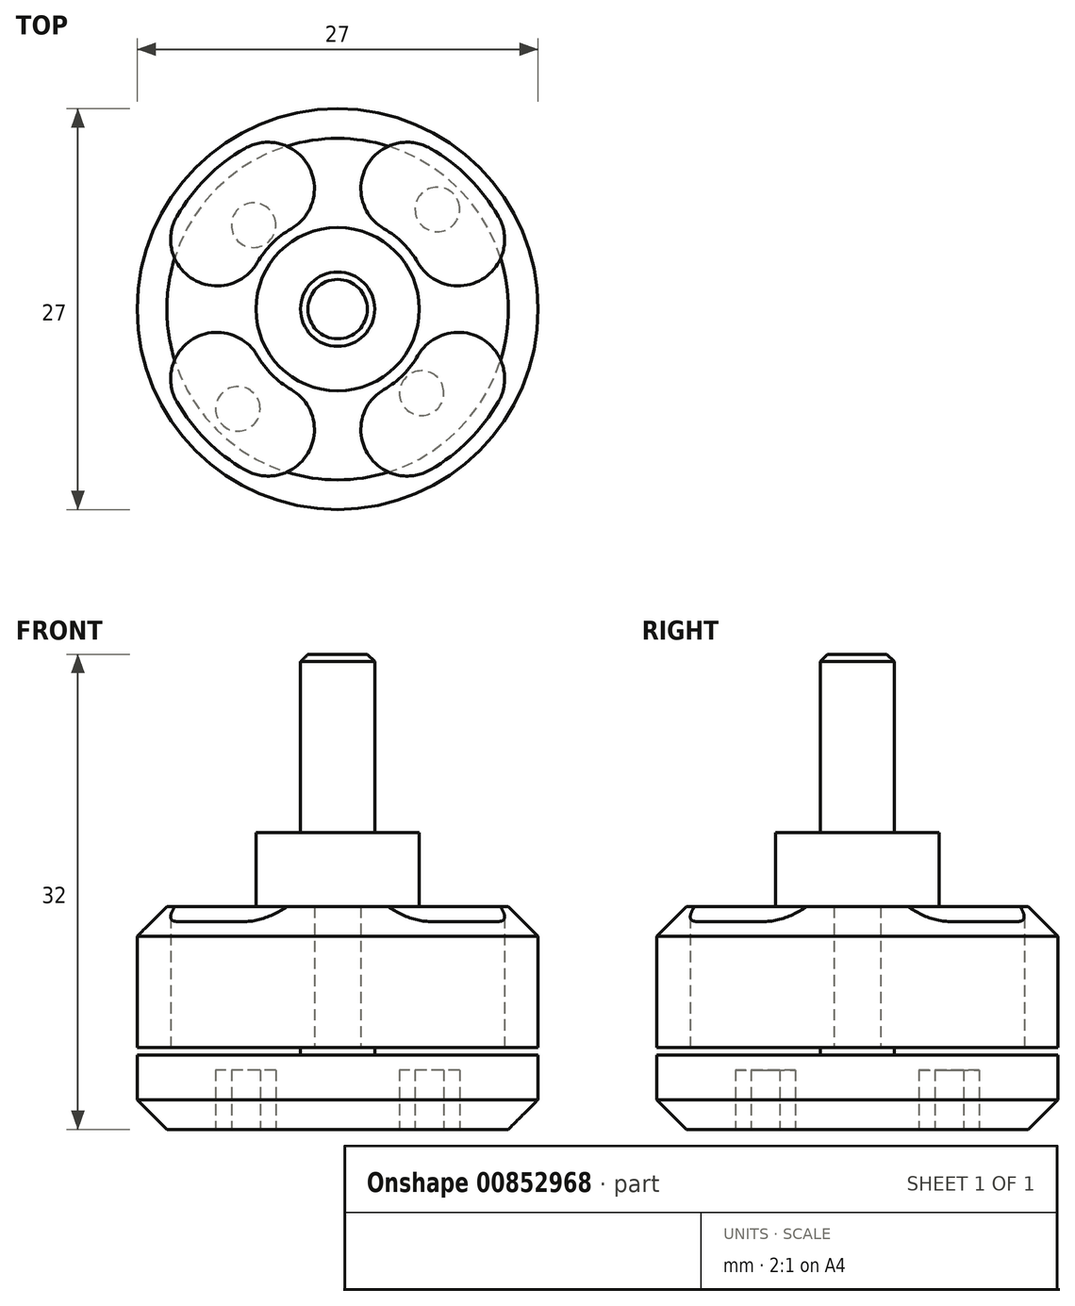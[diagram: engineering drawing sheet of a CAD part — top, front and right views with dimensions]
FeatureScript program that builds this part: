
annotation { "Feature Type Name" : "Feature", "Feature Type Description" : "" }
export const myFeature = defineFeature(function(context is Context, id is Id, definition is map)
    precondition{}
    {
        {
            var Q0;
            Q0=qCreatedBy(makeId("Front.planeOp"),FACE);
            var sketch = newSketch(context, id + "F0", { "sketchPlane" : qUnion([Q0])});
            skLineSegment(sketch, "E0", {"start": v(0, 0) * mm, "end": v(13.5, 0) * mm});
            skLineSegment(sketch, "E1", {"start": v(13.5, 0) * mm, "end": v(13.5, 5) * mm});
            skLineSegment(sketch, "E2", {"start": v(13.5, 15) * mm, "end": v(5.5, 15) * mm});
            skLineSegment(sketch, "E3", {"start": v(5.5, 15) * mm, "end": v(5.5, 20) * mm});
            skLineSegment(sketch, "E4", {"start": v(5.5, 20) * mm, "end": v(2.5, 20) * mm});
            skLineSegment(sketch, "E5", {"start": v(2.5, 20) * mm, "end": v(2.5, 32) * mm});
            skLineSegment(sketch, "E6", {"start": v(2.5, 32) * mm, "end": v(0, 32) * mm});
            skLineSegment(sketch, "E7", {"start": v(0, 32) * mm, "end": v(0, 0) * mm});
            skLineSegment(sketch, "E8", {"start": v(13.5, 5.5) * mm, "end": v(2.5, 5.5) * mm});
            skLineSegment(sketch, "E9", {"start": v(2.5, 5.5) * mm, "end": v(2.5, 5) * mm});
            skLineSegment(sketch, "E10", {"start": v(2.5, 5) * mm, "end": v(13.5, 5) * mm});
            skLineSegment(sketch, "E11.trimOffspring", {"start": v(13.5, 5.5) * mm, "end": v(13.5, 15) * mm});
            skSolve(sketch);
        }
        {
            var Q0;
            Q0 = qSketchRegion(id + "F0", true);
            var Q1;
            Q1=sQuery(id+"F0.wireOp",EDGE,"E7");
            revolve(context, id + "F1", {"surfaceOperationType" : NewSurfaceOperationType.NEW, "entities" : qUnion([Q0]), "axis" : qUnion([Q1]), "revolveType" : RevolveType.FULL});
        }
        {
            var Q0;
            Q0=makeQuery(id+"F1.opRevolve","SWEPT_EDGE",EDGE,{"disambiguationData":[OSD([sQuery(id+"F0.wireOp",EDGE,"E2"),sQuery(id+"F0.wireOp",EDGE,"E11.trimOffspring")])]});
            var Q1;
            Q1=makeQuery(id+"F1.opRevolve","SWEPT_EDGE",EDGE,{"disambiguationData":[OSD([sQuery(id+"F0.wireOp",EDGE,"E0"),sQuery(id+"F0.wireOp",EDGE,"E1")])]});
            chamfer(context, id + "F2", {"entities" : qUnion([Q0, Q1]), "width" : 2 * mm, "tangentPropagation" : true});
        }
        {
            var Q0;
            Q0=makeQuery(id+"F1.opRevolve","SWEPT_EDGE",EDGE,{"disambiguationData":[OSD([sQuery(id+"F0.wireOp",EDGE,"E5"),sQuery(id+"F0.wireOp",EDGE,"E6")])]});
            chamfer(context, id + "F3", {"entities" : qUnion([Q0]), "width" : 0.5 * mm, "tangentPropagation" : true});
        }
        {
            var Q0;
            Q0=qCreatedBy(makeId("Top.planeOp"),FACE);
            cPlane(context, id + "F4", {"entities" : qUnion([Q0]), "cplaneType" : CPlaneType.OFFSET, "offset" : 5 * mm, "width" : 150 * mm, "height" : 150 * mm});
        }
        {
            var Q0;
            Q0=qCreatedBy(id+"F4.planeOp",FACE);
            var sketch = newSketch(context, id + "F5", { "sketchPlane" : qUnion([Q0])});
            skArc(sketch, "E12", {"start": v(10.83, 6.25) * mm, "mid": v(8.84, 8.84) * mm, "end": v(6.25, 10.83) * mm});
            skArc(sketch, "E13", {"start": v(5.41, 3.12) * mm, "mid": v(4.42, 4.42) * mm, "end": v(3.12, 5.41) * mm});
            skLineSegment(sketch, "E14", {"start": v(3.12, 5.41) * mm, "end": v(6.25, 10.83) * mm, "construction": true});
            skLineSegment(sketch, "E15", {"start": v(5.41, 3.12) * mm, "end": v(10.83, 6.25) * mm, "construction": true});
            skArc(sketch, "E16", {"start": v(5.41, 3.12) * mm, "mid": v(9.68, 1.98) * mm, "end": v(10.83, 6.25) * mm});
            skArc(sketch, "E17", {"start": v(6.25, 10.83) * mm, "mid": v(1.98, 9.68) * mm, "end": v(3.12, 5.41) * mm});
            skArc(sketch, "E18.MirrorCS", {"start": v(-6.25, 10.83) * mm, "mid": v(-1.98, 9.68) * mm, "end": v(-3.12, 5.41) * mm});
            skArc(sketch, "E19.MirrorCS", {"start": v(-5.41, 3.12) * mm, "mid": v(-4.42, 4.42) * mm, "end": v(-3.12, 5.41) * mm});
            skArc(sketch, "E20.MirrorCS", {"start": v(-10.83, 6.25) * mm, "mid": v(-8.84, 8.84) * mm, "end": v(-6.25, 10.83) * mm});
            skArc(sketch, "E21.MirrorCS", {"start": v(-5.41, 3.12) * mm, "mid": v(-9.68, 1.98) * mm, "end": v(-10.83, 6.25) * mm});
            skArc(sketch, "E22.MirrorCS", {"start": v(-5.41, -3.12) * mm, "mid": v(-9.68, -1.98) * mm, "end": v(-10.83, -6.25) * mm});
            skArc(sketch, "E23.MirrorCS", {"start": v(-5.41, -3.12) * mm, "mid": v(-4.42, -4.42) * mm, "end": v(-3.12, -5.41) * mm});
            skArc(sketch, "E24.MirrorCS", {"start": v(-10.83, -6.25) * mm, "mid": v(-8.84, -8.84) * mm, "end": v(-6.25, -10.83) * mm});
            skArc(sketch, "E25.MirrorCS", {"start": v(-6.25, -10.83) * mm, "mid": v(-1.98, -9.68) * mm, "end": v(-3.12, -5.41) * mm});
            skArc(sketch, "E26.MirrorCS", {"start": v(6.25, -10.83) * mm, "mid": v(1.98, -9.68) * mm, "end": v(3.12, -5.41) * mm});
            skArc(sketch, "E27.MirrorCS", {"start": v(10.83, -6.25) * mm, "mid": v(8.84, -8.84) * mm, "end": v(6.25, -10.83) * mm});
            skArc(sketch, "E28.MirrorCS", {"start": v(5.41, -3.12) * mm, "mid": v(4.42, -4.42) * mm, "end": v(3.12, -5.41) * mm});
            skArc(sketch, "E29.MirrorCS", {"start": v(5.41, -3.12) * mm, "mid": v(9.68, -1.98) * mm, "end": v(10.83, -6.25) * mm});
            skSolve(sketch);
        }
        {
            var Q0;
            Q0 = qSketchRegion(id + "F5", true);
            extrude(context, id + "F6", {"entities" : qUnion([Q0]), "operationType" : NewBodyOperationType.REMOVE, "endBound" : BoundingType.THROUGH_ALL, "depth" : 25 * mm, "offsetDistance" : 25 * mm});
        }
        {
            var Q0;
            Q0=qCreatedBy(makeId("Top.planeOp"),FACE);
            var sketch = newSketch(context, id + "F7", { "sketchPlane" : qUnion([Q0])});
            skLineSegment(sketch, "E30", {"start": v(0, 0) * mm, "end": v(6.72, 6.72) * mm, "construction": true});
            skLineSegment(sketch, "E31", {"start": v(0, 0) * mm, "end": v(-5.66, 5.66) * mm, "construction": true});
            skCircle(sketch, "E32", {"center": v(-5.66, 5.66) * mm, "radius": 1.5 * mm});
            skCircle(sketch, "E33", {"center": v(6.72, 6.72) * mm, "radius": 1.5 * mm});
            skCircle(sketch, "E34.MirrorC", {"center": v(5.66, -5.66) * mm, "radius": 1.5 * mm});
            skCircle(sketch, "E35.MirrorC", {"center": v(-6.72, -6.72) * mm, "radius": 1.5 * mm});
            skSolve(sketch);
        }
        {
            var Q0;
            Q0 = qSketchRegion(id + "F7", true);
            extrude(context, id + "F8", {"entities" : qUnion([Q0]), "operationType" : NewBodyOperationType.REMOVE, "depth" : 4 * mm, "offsetDistance" : 25 * mm});
        }
    });
